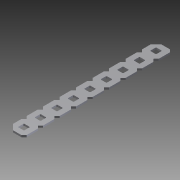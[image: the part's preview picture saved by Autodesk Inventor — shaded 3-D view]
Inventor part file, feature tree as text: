
AUTODESK INVENTOR PART (.ipt)
format: ipt  version: 2012 (Build 160160000, 160)  size: 554,496 bytes
history: native  units: in
note: dims shown in document units (in); Inventor stores cm internally (conversion verified against a paired STEP export)
features: plane x4, split x4, other x1, imported_body x1, fillet x1, sketch x1
ambient origin geometry x8: Origin, YZ Plane, XZ Plane, XY Plane, X Axis, Y Axis, Z Axis, Center Point
feature tree (12):
  parser-record x1  (decoder bookkeeping rows leaked as tree rows — omitted from the tree; the rows remain in map.json)
  imported_body  "Base1"
  plane  "Work Plane1"
  split  "Split1"
  plane  "Work Plane2"
  split  "Split2"
  fillet  "Fillet1"  [1 undecoded]
  sketch  "Sketch2"  dims[d1=-0.5in d3=0.02in d13=-0.0625in d14=-0.0625in]
  plane  "Work Plane5"
  split  "Split5"
  plane  "Work Plane6"
  split  "Split6"
note: 1 required parameter value undecoded (feature->parameter linkage not recoverable at this tier; creation-order binding heuristic only, values carry confidence <= 0.55)
